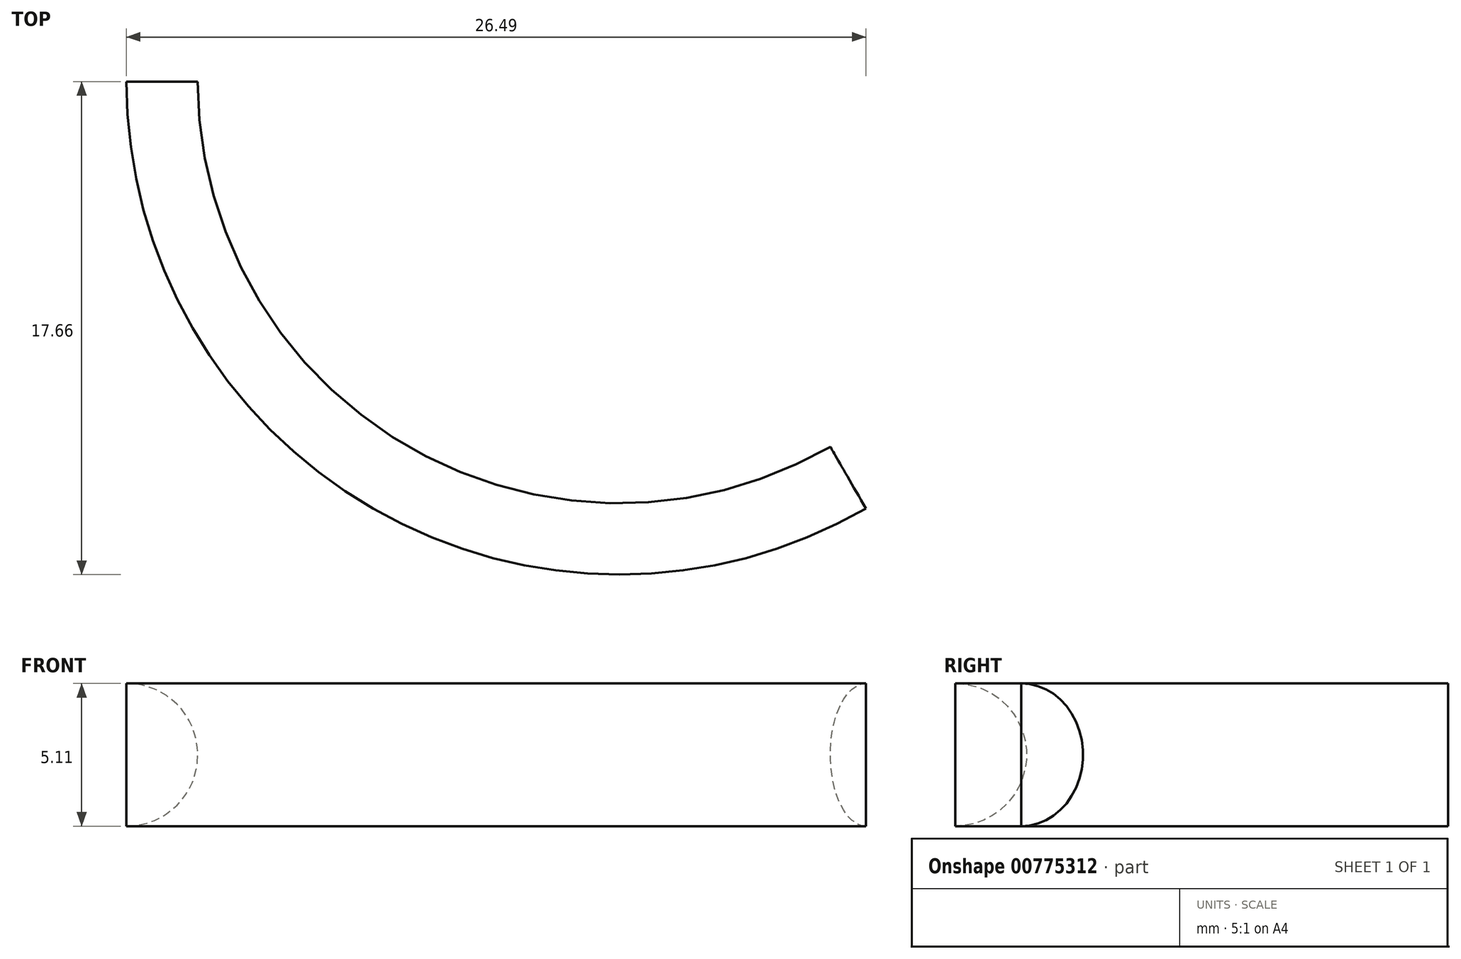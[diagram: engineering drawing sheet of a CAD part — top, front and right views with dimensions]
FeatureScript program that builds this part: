
annotation { "Feature Type Name" : "Feature", "Feature Type Description" : "" }
export const myFeature = defineFeature(function(context is Context, id is Id, definition is map)
    precondition{}
    {
        {
            var Q0;
            Q0=qCreatedBy(makeId("Front.planeOp"),FACE);
            var sketch = newSketch(context, id + "F0", { "sketchPlane" : qUnion([Q0])});
            skLineSegment(sketch, "E0", {"start": v(4.31, -2.33) * mm, "end": v(4.31, 2.78) * mm});
            skArc(sketch, "E1", {"start": v(4.31, -2.33) * mm, "mid": v(6.87, 0.23) * mm, "end": v(4.31, 2.78) * mm});
            skLineSegment(sketch, "E2", {"start": v(4.31, -2.33) * mm, "end": v(21.97, -2.33) * mm});
            skLineSegment(sketch, "E3", {"start": v(21.97, -2.33) * mm, "end": v(21.97, 15.66) * mm});
            skSolve(sketch);
        }
        {
            var Q0;
            Q0 = qSketchRegion(id + "F0", true);
            var Q1;
            Q1=sQuery(id+"F0.wireOp",EDGE,"E3");
            revolve(context, id + "F1", {"surfaceOperationType" : NewSurfaceOperationType.NEW, "entities" : qUnion([Q0]), "axis" : qUnion([Q1]), "revolveType" : RevolveType.ONE_DIRECTION, "angle" : 120 * degree});
        }
    });
